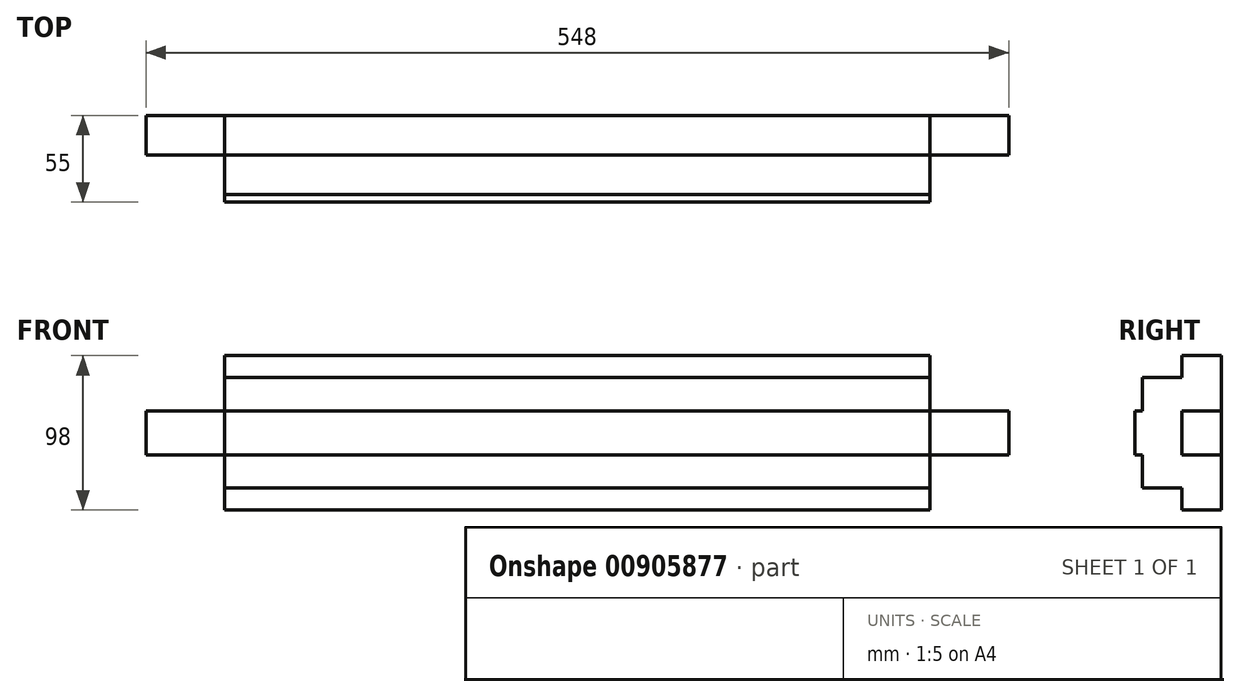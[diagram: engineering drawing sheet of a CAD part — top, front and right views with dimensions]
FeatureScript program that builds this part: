
annotation { "Feature Type Name" : "Feature", "Feature Type Description" : "" }
export const myFeature = defineFeature(function(context is Context, id is Id, definition is map)
    precondition{}
    {
        {
            var Q0;
            Q0=qCreatedBy(makeId("Front.planeOp"),FACE);
            var sketch = newSketch(context, id + "F0", { "sketchPlane" : qUnion([Q0])});
            skLineSegment(sketch, "E0.bottom", {"start": v(224, -49) * mm, "end": v(-224, -49) * mm});
            skLineSegment(sketch, "E0.top", {"start": v(224, 49) * mm, "end": v(-224, 49) * mm});
            skLineSegment(sketch, "E0.left", {"start": v(274, -14) * mm, "end": v(274, 14) * mm});
            skLineSegment(sketch, "E0.right", {"start": v(-274, -14) * mm, "end": v(-274, 14) * mm});
            skPoint(sketch, "E0.middle", {"position": v(0, 0) * mm});
            skLineSegment(sketch, "E1.top", {"start": v(-274, 14) * mm, "end": v(-224, 14) * mm});
            skLineSegment(sketch, "E1.right", {"start": v(-224, 49) * mm, "end": v(-224, 14) * mm});
            skLineSegment(sketch, "E2.top", {"start": v(-274, -14) * mm, "end": v(-224, -14) * mm});
            skLineSegment(sketch, "E2.right", {"start": v(-224, -49) * mm, "end": v(-224, -14) * mm});
            skLineSegment(sketch, "E3.top", {"start": v(274, 14) * mm, "end": v(224, 14) * mm});
            skLineSegment(sketch, "E3.right", {"start": v(224, 49) * mm, "end": v(224, 14) * mm});
            skLineSegment(sketch, "E4.top", {"start": v(274, -14) * mm, "end": v(224, -14) * mm});
            skLineSegment(sketch, "E4.right", {"start": v(224, -49) * mm, "end": v(224, -14) * mm});
            skPoint(sketch, "E5.orphan", {"position": v(-274, 49) * mm});
            skPoint(sketch, "E2.left.start.orphan", {"position": v(-274, -49) * mm});
            skPoint(sketch, "E6.orphan", {"position": v(274, 49) * mm});
            skPoint(sketch, "E7.orphan", {"position": v(274, -49) * mm});
            skLineSegment(sketch, "E8", {"start": v(-224, 14) * mm, "end": v(-224, 35) * mm});
            skLineSegment(sketch, "E9", {"start": v(-224, 35) * mm, "end": v(224, 35) * mm});
            skLineSegment(sketch, "E10", {"start": v(224, 35) * mm, "end": v(224, 14) * mm});
            skLineSegment(sketch, "E11", {"start": v(-224, 14) * mm, "end": v(224, 14) * mm});
            skLineSegment(sketch, "E12", {"start": v(224, -14) * mm, "end": v(-224, -14) * mm});
            skLineSegment(sketch, "E13", {"start": v(-224, -14) * mm, "end": v(-224, -35) * mm});
            skLineSegment(sketch, "E14", {"start": v(-224, -35) * mm, "end": v(224, -35) * mm});
            skLineSegment(sketch, "E15", {"start": v(224, -14) * mm, "end": v(224, 14) * mm});
            skLineSegment(sketch, "E16", {"start": v(-224, -14) * mm, "end": v(-224, 14) * mm});
            skSolve(sketch);
        }
        {
            var Q0;
            Q0 = qSketchRegion(id + "F0", true);
            extrude(context, id + "F1", {"entities" : qUnion([Q0]), "depth" : 25 * mm, "offsetDistance" : 25 * mm});
        }
        {
            var Q0;
            Q0=makeQuery(id+"F1.opExtrude","CAP_FACE",FACE,{"disambiguationData":[OSD([sQuery(id+"F0.wireOp",EDGE,"E0.bottom"),sQuery(id+"F0.wireOp",EDGE,"E0.top"),sQuery(id+"F0.wireOp",EDGE,"E0.left"),sQuery(id+"F0.wireOp",EDGE,"E0.right"),sQuery(id+"F0.wireOp",EDGE,"E1.top"),sQuery(id+"F0.wireOp",EDGE,"E1.right"),sQuery(id+"F0.wireOp",EDGE,"E2.top"),sQuery(id+"F0.wireOp",EDGE,"E2.right"),sQuery(id+"F0.wireOp",EDGE,"E3.top"),sQuery(id+"F0.wireOp",EDGE,"E3.right"),sQuery(id+"F0.wireOp",EDGE,"E4.top"),sQuery(id+"F0.wireOp",EDGE,"E4.right"),sQuery(id+"F0.wireOp",EDGE,"E8"),sQuery(id+"F0.wireOp",EDGE,"E10"),sQuery(id+"F0.wireOp",EDGE,"E13")])],"isStart":false});
            var sketch = newSketch(context, id + "F2", { "sketchPlane" : qUnion([Q0])});
            skLineSegment(sketch, "E17.bottom", {"start": v(-224, 14) * mm, "end": v(224, 14) * mm});
            skLineSegment(sketch, "E17.top", {"start": v(-224, 35) * mm, "end": v(224, 35) * mm});
            skLineSegment(sketch, "E17.left", {"start": v(-224, 14) * mm, "end": v(-224, 35) * mm});
            skLineSegment(sketch, "E17.right", {"start": v(224, 14) * mm, "end": v(224, 35) * mm});
            skLineSegment(sketch, "E18.bottom", {"start": v(-224, -14) * mm, "end": v(224, -14) * mm});
            skLineSegment(sketch, "E18.top", {"start": v(-224, -35) * mm, "end": v(224, -35) * mm});
            skLineSegment(sketch, "E18.left", {"start": v(-224, -14) * mm, "end": v(-224, -35) * mm});
            skLineSegment(sketch, "E18.right", {"start": v(224, -14) * mm, "end": v(224, -35) * mm});
            skSolve(sketch);
        }
        {
            var Q0;
            Q0 = qSketchRegion(id + "F2", true);
            extrude(context, id + "F3", {"entities" : qUnion([Q0]), "operationType" : NewBodyOperationType.ADD, "depth" : 25 * mm, "offsetDistance" : 25 * mm});
        }
        {
            var Q0;
            {var subQ0=sQuery(id+"F0.wireOp",EDGE,"E4.right");var subQ1=sQuery(id+"F0.wireOp",EDGE,"E4.top");var subQ2=sQuery(id+"F0.wireOp",EDGE,"E10");var subQ3=sQuery(id+"F0.wireOp",EDGE,"E3.right");var subQ4=sQuery(id+"F0.wireOp",EDGE,"E3.top");var subQ5=sQuery(id+"F0.wireOp",EDGE,"E13");var subQ6=sQuery(id+"F0.wireOp",EDGE,"E2.right");var subQ7=sQuery(id+"F0.wireOp",EDGE,"E2.top");var subQ8=sQuery(id+"F0.wireOp",EDGE,"E0.left");var subQ9=sQuery(id+"F0.wireOp",EDGE,"E0.right");var subQ10=sQuery(id+"F0.wireOp",EDGE,"E1.top");var subQ11=sQuery(id+"F0.wireOp",EDGE,"E8");var subQ12=sQuery(id+"F0.wireOp",EDGE,"E1.right");Q0=makeQuery(id+"F3.boolean.opBoolean","SPLIT",FACE,{"disambiguationData":[TD([makeQuery(id+"F1.opExtrude","SWEPT_FACE",FACE,{"disambiguationData":[OSD([subQ8])]})])],"derivedFrom":makeQuery(id+"F1.opExtrude","CAP_FACE",FACE,{"disambiguationData":[OSD([sQuery(id+"F0.wireOp",EDGE,"E0.bottom"),sQuery(id+"F0.wireOp",EDGE,"E0.top"),subQ8,subQ9,subQ10,subQ12,subQ7,subQ6,subQ4,subQ3,subQ1,subQ0,subQ11,subQ2,subQ5])],"isStart":false})});}
            var sketch = newSketch(context, id + "F4", { "sketchPlane" : qUnion([Q0])});
            skLineSegment(sketch, "E19.bottom", {"start": v(-224, 14) * mm, "end": v(224, 14) * mm});
            skLineSegment(sketch, "E19.top", {"start": v(-224, -14) * mm, "end": v(224, -14) * mm});
            skLineSegment(sketch, "E19.left", {"start": v(-224, 14) * mm, "end": v(-224, -14) * mm});
            skLineSegment(sketch, "E19.right", {"start": v(224, 14) * mm, "end": v(224, -14) * mm});
            skSolve(sketch);
        }
        {
            var Q0;
            Q0 = qSketchRegion(id + "F4", true);
            extrude(context, id + "F5", {"entities" : qUnion([Q0]), "operationType" : NewBodyOperationType.ADD, "depth" : 30 * mm, "offsetDistance" : 25 * mm});
        }
    });
